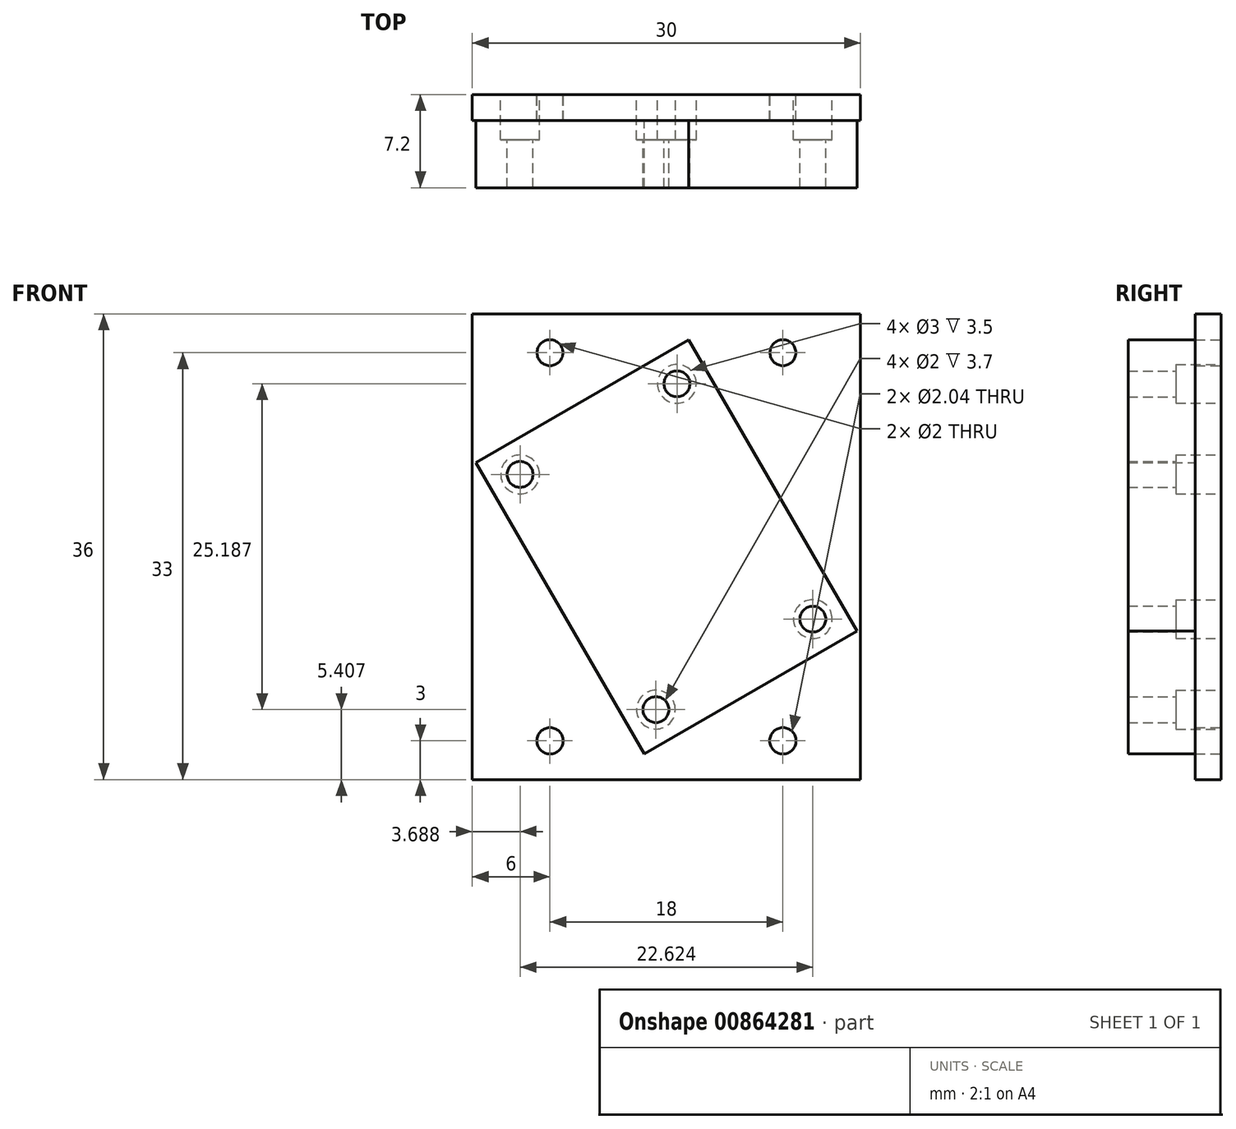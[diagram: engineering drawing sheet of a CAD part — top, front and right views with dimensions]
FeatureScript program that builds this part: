
annotation { "Feature Type Name" : "Feature", "Feature Type Description" : "" }
export const myFeature = defineFeature(function(context is Context, id is Id, definition is map)
    precondition{}
    {
        {
            var Q0;
            Q0=qCreatedBy(makeId("Front.planeOp"),FACE);
            var sketch = newSketch(context, id + "F0", { "sketchPlane" : qUnion([Q0])});
            skLineSegment(sketch, "E0.bottom", {"start": v(-15, 18) * mm, "end": v(15, 18) * mm});
            skLineSegment(sketch, "E0.top", {"start": v(-15, -18) * mm, "end": v(15, -18) * mm});
            skLineSegment(sketch, "E0.left", {"start": v(-15, 18) * mm, "end": v(-15, -18) * mm});
            skLineSegment(sketch, "E0.right", {"start": v(15, 18) * mm, "end": v(15, -18) * mm});
            skCircle(sketch, "E1", {"center": v(-11.31, 5.6) * mm, "radius": 1 * mm});
            skCircle(sketch, "E2", {"center": v(-0.81, -12.6) * mm, "radius": 1 * mm});
            skCircle(sketch, "E3", {"center": v(0.81, 12.6) * mm, "radius": 1 * mm});
            skCircle(sketch, "E4", {"center": v(11.31, -5.6) * mm, "radius": 1 * mm});
            skPoint(sketch, "E5.endSnap0", {"position": v(15, 0) * mm});
            skLineSegment(sketch, "E6", {"start": v(5.37, 18) * mm, "end": v(-11.37, 18) * mm});
            skCircle(sketch, "E7", {"center": v(-9, 15) * mm, "radius": 1 * mm});
            skCircle(sketch, "E8", {"center": v(9, 15) * mm, "radius": 1 * mm});
            skCircle(sketch, "E9", {"center": v(-9, -15) * mm, "radius": 1.02 * mm});
            skCircle(sketch, "E10", {"center": v(9, -15) * mm, "radius": 1.02 * mm});
            skSolve(sketch);
        }
        {
            var Q0;
            Q0=makeQuery(id+"F0.imprint","IMPRINT",FACE,{"disambiguationData":[TD([[makeQuery(id+"F0.imprint","IMPRINT",EDGE,{"derivedFrom":sQuery(id+"F0.wireOp",EDGE,"E0.top")}),1.0]])]});
            extrude(context, id + "F1", {"entities" : qUnion([Q0]), "depth" : 2 * mm, "offsetDistance" : 25 * mm});
        }
        {
            var Q0;
            Q0=makeQuery(id+"F1.opExtrude","CAP_FACE",FACE,{"disambiguationData":[OSD([sQuery(id+"F0.wireOp",EDGE,"E0.bottom"),sQuery(id+"F0.wireOp",EDGE,"E0.top"),sQuery(id+"F0.wireOp",EDGE,"E0.left"),sQuery(id+"F0.wireOp",EDGE,"E0.right"),sQuery(id+"F0.wireOp",EDGE,"E1"),sQuery(id+"F0.wireOp",EDGE,"E2"),sQuery(id+"F0.wireOp",EDGE,"E3"),sQuery(id+"F0.wireOp",EDGE,"E4"),sQuery(id+"F0.wireOp",EDGE,"E6"),sQuery(id+"F0.wireOp",EDGE,"E7"),sQuery(id+"F0.wireOp",EDGE,"E8"),sQuery(id+"F0.wireOp",EDGE,"E9"),sQuery(id+"F0.wireOp",EDGE,"E10")])],"isStart":false});
            var sketch = newSketch(context, id + "F2", { "sketchPlane" : qUnion([Q0])});
            skLineSegment(sketch, "E11", {"start": v(1.73, 16) * mm, "end": v(-14.73, 6.5) * mm});
            skLineSegment(sketch, "E12", {"start": v(-14.73, 6.5) * mm, "end": v(-1.73, -16) * mm});
            skLineSegment(sketch, "E13", {"start": v(-1.73, -16) * mm, "end": v(14.73, -6.5) * mm});
            skLineSegment(sketch, "E14", {"start": v(14.73, -6.5) * mm, "end": v(1.73, 16) * mm});
            skSolve(sketch);
        }
        {
            var Q0;
            Q0=makeQuery(id+"F2.imprint","IMPRINT",FACE,{"disambiguationData":[TD([[makeQuery(id+"F2.imprint","IMPRINT",EDGE,{"derivedFrom":makeQuery(id+"F1.opExtrude","CAP_EDGE",EDGE,{"disambiguationData":[OSD([sQuery(id+"F0.wireOp",EDGE,"E1")])],"isStart":false})}),1.0]])]});
            var Q1;
            Q1=makeQuery(id+"F2.imprint","IMPRINT",FACE,{"disambiguationData":[TD([[makeQuery(id+"F2.imprint","IMPRINT",EDGE,{"derivedFrom":makeQuery(id+"F1.opExtrude","CAP_EDGE",EDGE,{"disambiguationData":[OSD([sQuery(id+"F0.wireOp",EDGE,"E2")])],"isStart":false})}),1.0]])]});
            var Q2;
            Q2=makeQuery(id+"F2.imprint","IMPRINT",FACE,{"disambiguationData":[TD([[makeQuery(id+"F2.imprint","IMPRINT",EDGE,{"derivedFrom":makeQuery(id+"F1.opExtrude","CAP_EDGE",EDGE,{"disambiguationData":[OSD([sQuery(id+"F0.wireOp",EDGE,"E3")])],"isStart":false})}),1.0]])]});
            var Q3;
            Q3=makeQuery(id+"F2.imprint","IMPRINT",FACE,{"disambiguationData":[TD([[makeQuery(id+"F2.imprint","IMPRINT",EDGE,{"derivedFrom":makeQuery(id+"F1.opExtrude","CAP_EDGE",EDGE,{"disambiguationData":[OSD([sQuery(id+"F0.wireOp",EDGE,"E4")])],"isStart":false})}),1.0]])]});
            var Q4;
            Q4=makeQuery(id+"F2.imprint","IMPRINT",FACE,{"disambiguationData":[TD([[makeQuery(id+"F2.imprint","IMPRINT",EDGE,{"derivedFrom":sQuery(id+"F2.wireOp",EDGE,"E11")}),1.0]])]});
            extrude(context, id + "F3", {"entities" : qUnion([Q0, Q1, Q2, Q3, Q4]), "operationType" : NewBodyOperationType.ADD, "depth" : 5.2 * mm, "offsetDistance" : 25 * mm});
        }
        {
            var Q0;
            Q0=makeQuery(id+"F1.opExtrude","CAP_FACE",FACE,{"disambiguationData":[OSD([sQuery(id+"F0.wireOp",EDGE,"E0.bottom"),sQuery(id+"F0.wireOp",EDGE,"E0.top"),sQuery(id+"F0.wireOp",EDGE,"E0.left"),sQuery(id+"F0.wireOp",EDGE,"E0.right"),sQuery(id+"F0.wireOp",EDGE,"E1"),sQuery(id+"F0.wireOp",EDGE,"E2"),sQuery(id+"F0.wireOp",EDGE,"E3"),sQuery(id+"F0.wireOp",EDGE,"E4"),sQuery(id+"F0.wireOp",EDGE,"E6"),sQuery(id+"F0.wireOp",EDGE,"E7"),sQuery(id+"F0.wireOp",EDGE,"E8"),sQuery(id+"F0.wireOp",EDGE,"E9"),sQuery(id+"F0.wireOp",EDGE,"E10")])],"isStart":true});
            var sketch = newSketch(context, id + "F4", { "sketchPlane" : qUnion([Q0])});
            skCircle(sketch, "E15", {"center": v(-11.31, -5.6) * mm, "radius": 1.5 * mm});
            skCircle(sketch, "E16", {"center": v(-0.81, 12.6) * mm, "radius": 1.5 * mm});
            skCircle(sketch, "E17", {"center": v(11.31, 5.6) * mm, "radius": 1.5 * mm});
            skCircle(sketch, "E18", {"center": v(0.81, -12.6) * mm, "radius": 1.5 * mm});
            skSolve(sketch);
        }
        {
            var Q0;
            Q0=makeQuery(id+"F4.imprint","IMPRINT",FACE,{"disambiguationData":[TD([[makeQuery(id+"F4.imprint","IMPRINT",EDGE,{"derivedFrom":sQuery(id+"F4.wireOp",EDGE,"E15")}),1.0]])]});
            var Q1;
            Q1=makeQuery(id+"F4.imprint","IMPRINT",FACE,{"disambiguationData":[TD([[makeQuery(id+"F4.imprint","IMPRINT",EDGE,{"derivedFrom":sQuery(id+"F4.wireOp",EDGE,"E18")}),1.0]])]});
            var Q2;
            Q2=makeQuery(id+"F4.imprint","IMPRINT",FACE,{"disambiguationData":[TD([[makeQuery(id+"F4.imprint","IMPRINT",EDGE,{"derivedFrom":sQuery(id+"F4.wireOp",EDGE,"E16")}),1.0]])]});
            var Q3;
            Q3=makeQuery(id+"F4.imprint","IMPRINT",FACE,{"disambiguationData":[TD([[makeQuery(id+"F4.imprint","IMPRINT",EDGE,{"derivedFrom":sQuery(id+"F4.wireOp",EDGE,"E17")}),1.0]])]});
            extrude(context, id + "F5", {"entities" : qUnion([Q0, Q1, Q2, Q3]), "operationType" : NewBodyOperationType.REMOVE, "depth" : -3.5 * mm, "offsetDistance" : 25 * mm});
        }
        {
            var Q0;
            Q0=makeQuery(id+"F1.opExtrude","CAP_FACE",FACE,{"disambiguationData":[OSD([sQuery(id+"F0.wireOp",EDGE,"E0.bottom"),sQuery(id+"F0.wireOp",EDGE,"E0.top"),sQuery(id+"F0.wireOp",EDGE,"E0.left"),sQuery(id+"F0.wireOp",EDGE,"E0.right"),sQuery(id+"F0.wireOp",EDGE,"E1"),sQuery(id+"F0.wireOp",EDGE,"E2"),sQuery(id+"F0.wireOp",EDGE,"E3"),sQuery(id+"F0.wireOp",EDGE,"E4"),sQuery(id+"F0.wireOp",EDGE,"E6"),sQuery(id+"F0.wireOp",EDGE,"E7"),sQuery(id+"F0.wireOp",EDGE,"E8"),sQuery(id+"F0.wireOp",EDGE,"E9"),sQuery(id+"F0.wireOp",EDGE,"E10")])],"isStart":true});
            var sketch = newSketch(context, id + "F6", { "sketchPlane" : qUnion([Q0])});
            skCircle(sketch, "E19", {"center": v(-11.31, -5.6) * mm, "radius": 1 * mm});
            skCircle(sketch, "E20", {"center": v(-0.81, 12.6) * mm, "radius": 1 * mm});
            skCircle(sketch, "E21", {"center": v(11.31, 5.6) * mm, "radius": 1 * mm});
            skCircle(sketch, "E22", {"center": v(0.81, -12.6) * mm, "radius": 1 * mm});
            skSolve(sketch);
        }
        {
            var Q0;
            Q0=makeQuery(id+"F6.imprint","IMPRINT",FACE,{"disambiguationData":[TD([[makeQuery(id+"F6.imprint","IMPRINT",EDGE,{"derivedFrom":sQuery(id+"F6.wireOp",EDGE,"E20")}),1.0]])]});
            var Q1;
            Q1=makeQuery(id+"F6.imprint","IMPRINT",FACE,{"disambiguationData":[TD([[makeQuery(id+"F6.imprint","IMPRINT",EDGE,{"derivedFrom":sQuery(id+"F6.wireOp",EDGE,"E21")}),1.0]])]});
            var Q2;
            Q2=makeQuery(id+"F6.imprint","IMPRINT",FACE,{"disambiguationData":[TD([[makeQuery(id+"F6.imprint","IMPRINT",EDGE,{"derivedFrom":sQuery(id+"F6.wireOp",EDGE,"E22")}),1.0]])]});
            var Q3;
            Q3=makeQuery(id+"F6.imprint","IMPRINT",FACE,{"disambiguationData":[TD([[makeQuery(id+"F6.imprint","IMPRINT",EDGE,{"derivedFrom":sQuery(id+"F6.wireOp",EDGE,"E19")}),1.0]])]});
            extrude(context, id + "F7", {"entities" : qUnion([Q0, Q1, Q2, Q3]), "operationType" : NewBodyOperationType.REMOVE, "oppositeDirection" : true, "depth" : 10 * mm, "offsetDistance" : 25 * mm});
        }
    });
